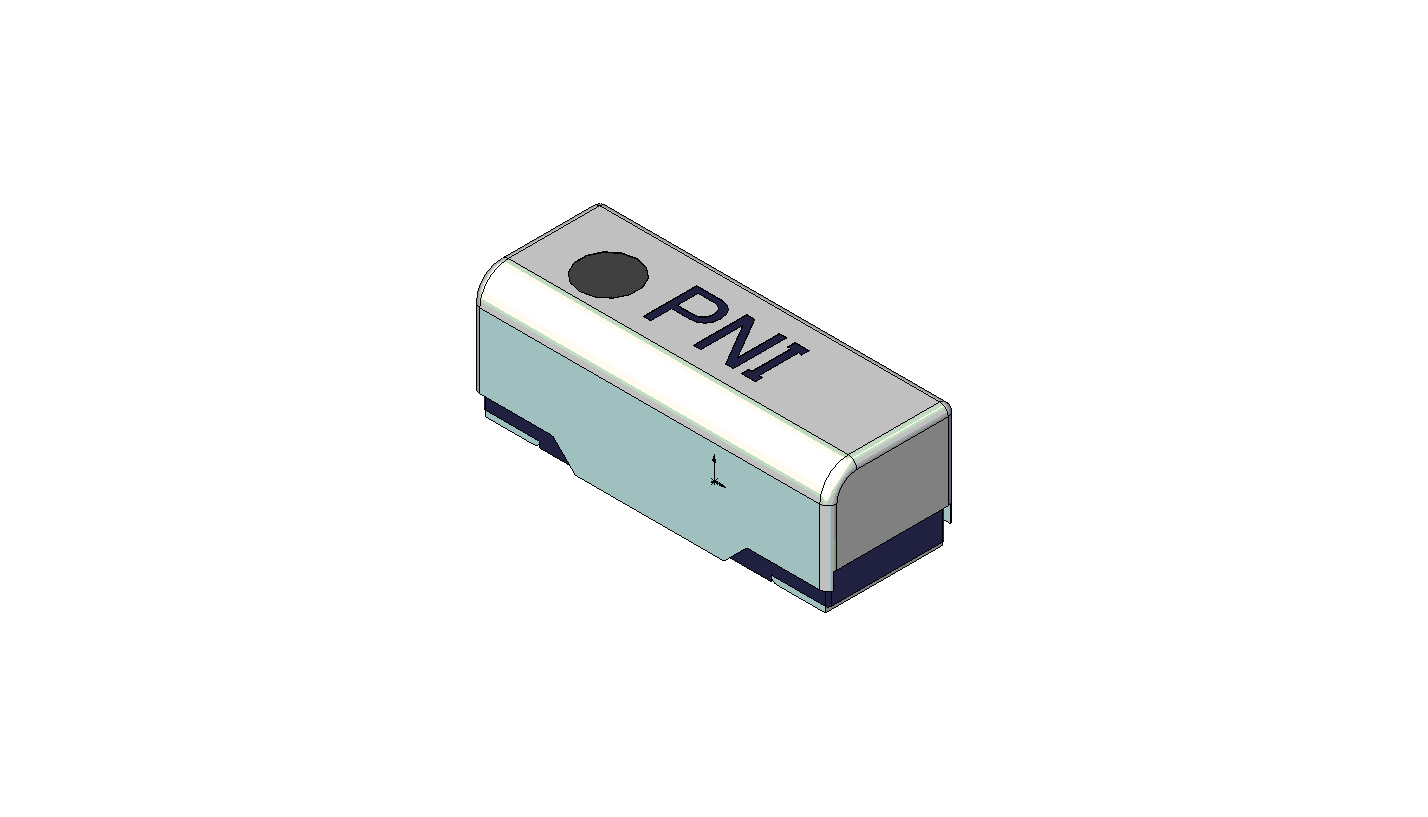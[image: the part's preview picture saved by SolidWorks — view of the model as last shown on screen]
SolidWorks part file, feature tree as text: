
SOLIDWORKS PART (.sldprt)
format: sldprt  version: not decoded by parser v0  size: 776,704 bytes
history: native  units: mm
features: sketch x8, cut_extrude x5, fillet x4, extrude x3, material x1, shell x1 (+10 scaffold rows collapsed)
feature tree (32):
  scaffold x10  (default folders/planes/origin — collapsed)
  material  "Material <not specified>"
  sketch  "Sketch1"  dims[D1=6.25mm D2=2.25mm]
  extrude  "Base-Extrude"  Depth=2.2mm
  sketch  "Sketch2"  dims[c1.D1=2.6mm c1.D2=~0.74212mm c2.D2=135.0deg c2.D3=1.8mm]
  cut_extrude  "Cut-Extrude1"  [1 undecoded]
  fillet  "Fillet1"  Radius=0.15mm
  fillet  "Fillet2"  Radius=0.5mm
  shell  "Shell1"  Thickness=0.1mm
  sketch  "Sketch4"  dims[D1=0.1mm]
  cut_extrude  "Cut-Extrude2"  Depth=0.1mm
  sketch  "Sketch7"  dims[c1.D1=1.5mm c1.D2=2.0mm c2.D1=1.5mm c2.D2=2.05mm]
  cut_extrude  "Cut-Extrude4"  [1 undecoded]
  sketch  "Sketch6"  dims[D2=1.0mm D1=0.85mm D3=2.0mm]
  cut_extrude  "Cut-Extrude3"  Depth=0.01mm
  sketch  "Sketch8"  dims[D1=0.1mm]
  extrude  "Extrude1"  [1 undecoded]
  sketch  "Sketch9"  dims[D1=1.0mm]
  cut_extrude  "Cut-Extrude5"  Depth=0.1mm
  sketch  "Sketch10"
  extrude  "Extrude2"  Depth=0.1mm
  fillet  "Fillet4"  Radius=0.1mm
  fillet  "Fillet5"  Radius=0.1mm
decode coverage: 17 of 21 modeling features carry decoded parameters
note: ~ marks probable driven/reference dimensions
note: 3 parameter values undecoded
summary: no parameter record found for 3 features
note: suppression state not decoded; provenance and decode notes live in map.json
